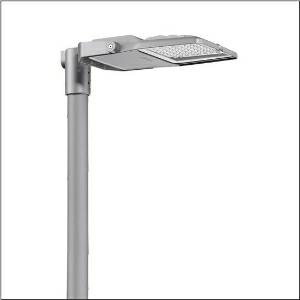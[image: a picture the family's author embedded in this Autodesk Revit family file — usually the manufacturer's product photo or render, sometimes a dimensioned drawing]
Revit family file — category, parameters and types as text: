
# Revit family: floodlight_fl_21_iq_mini___pl52_5xa7772d2d3a_9966
name_source: partatom
category: Lighting Fixtures
units: mm (PartAtom-declared; Revit-internal decimal feet)

## family parameters
Cut with Voids When Loaded = No
Host = Face
Light Source = No
Part Type = Normal
Room Calculation Point = No
Round Connector Dimension = Use Diameter
Shared = No

## types (1)
- --- (1 x LED, 17830 lm, 143 W, 3000K)
    Apparent Load = 143 VA
    CIE Flux Codes = 26 60 98 100 100
    Color Rendering = 70
    Color Temperature = 3000K
    Default Elevation = 1800 mm
    Description = Floodlight FL 21 iQ mini, floodlight, primary light control with lens, of PMMA, primary optical cover: protective disc, of toughened safety glass, transparent, light distribution: PL52, light emission: direct distribution, installation type: surface-mounted, lamps: LED, High Power LED, rated values: 17.830lm | 143W | 124,7lm/W (begin service life); end service life: 17.830lm | 151,6W; at 50% lumin. flux: 8.915lm | 60,6W | 147,1lm/W, colour temperature: 3000K, colour rendering: CRI > 70, light colour: 730, light setting 1 begin service life: 100% | 17.830lm | 143W | 124,7lm/W | 3.000K, light setting 1 end service life: 151,6W, further light settings possible, control: pre-setting: linear dimming characteristic, Auto-Match, Temp-Guard, Night-Set, Smart-Wire, Desk-Remote (wireless, voltage-free reading and setting of iQ features in the workshop via application-optimized NFC function/RFID function), optimised constant luminous flux control (CLO 2.0), Light-Fading, Lumen-Switch, with terminal, 6-pole, mains connection: 220..240V, AC, 50/60Hz, luminaire housing, of diecast aluminium, powder-coated, SITECO metallic grey (DB 702S), corrosivity category C5 mid according to DIN EN ISO 12944suitable for swimming poolschlorine-resistant, sealing non-destructively replaceable, please order mast flange separately, mast bracket, of steel, galvanised, powder-coated, protection rating (complete): IP66, insulation class (complete): insulation class II (safety insulation), certification: CE, ENEC, VDE, protection symbol: D, impact resistance: IK08, permissible operating ambient temperature: -40..+40°C, permissible operating ambient temperature for outdoor applications: -40..+50°C, standard: DIN EN 12944, LABS conformity tested according to VDMA 24364:2018-05, packaging unit: 1 piece

Light Distribution: PL52
    Height = 70 mm
    Lamp = 1 x LED
    Lamp Light Flux = 17830 lm
    Lamp Power = 143 W
    Lamp count = 1
    Length = 485 mm
    Luminous efficacy = 125 lm/W
    Manufacturer = Siteco
    ModVariant = No
    Model = 5XA7772D2D3A
    Number of Poles = 1
    OnlyDefault = Yes
    Power Factor = 1
    Product Name = Floodlight FL 21 iQ mini | PL52
    Product group = floodlight | pylon annexe
    ProductGroupID = 6201
    Protection Class = Protection class II
    Protection Degree = IP 66
    RLX_Detail_Level = 1
    RLX_Emergency_Light_Flux = 0 lm
    RLX_Emergency_Type = 0
    RLX_Emergency_Type_DB = No
    RlxData = <blob elided: 102057 chars, md5=1f128b2c>
    Socket = socket
    Standby Power = 0 W
    System Light Flux = 17830 lm
    System Power = 143 W
    Type Comments = factory setting: luminous flux: 100 % | dim-lin: 254 | 730 mA
    Type Image = l_1007125.jpg
    URL = http://relux.com
    VarID = @adj_163181
    Voltage = 0 V
    Weight = 0.00 kg
    Width = 337 mm

## geometry (parser evidence)
native form markers: Blend x4, Sweep x12
no freeform markers — native parametric forms only
